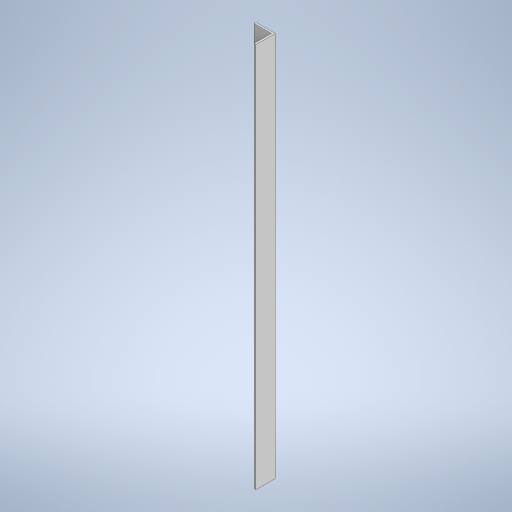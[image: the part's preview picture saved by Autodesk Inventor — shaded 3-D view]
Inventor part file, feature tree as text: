
AUTODESK INVENTOR PART (.ipt)
format: ipt  version: 2024 (Build 280153000, 153)  size: 237,056 bytes
history: native  units: mm
features: extrude x1, sketch x1
ambient origin geometry x8: Origin, YZ Plane, XZ Plane, XY Plane, X Axis, Y Axis, Z Axis, Center Point
bodies: Solid1 (feature_tree)
feature tree (2):
  extrude  "Extrusion1"  Depth=50.0mm
  sketch  "Sketch1"  dims[d2=5.0mm d3=50.0mm d4=50.0mm d5=45.0mm d6=5.0mm d7=1000.0mm d8=0.0mm]
